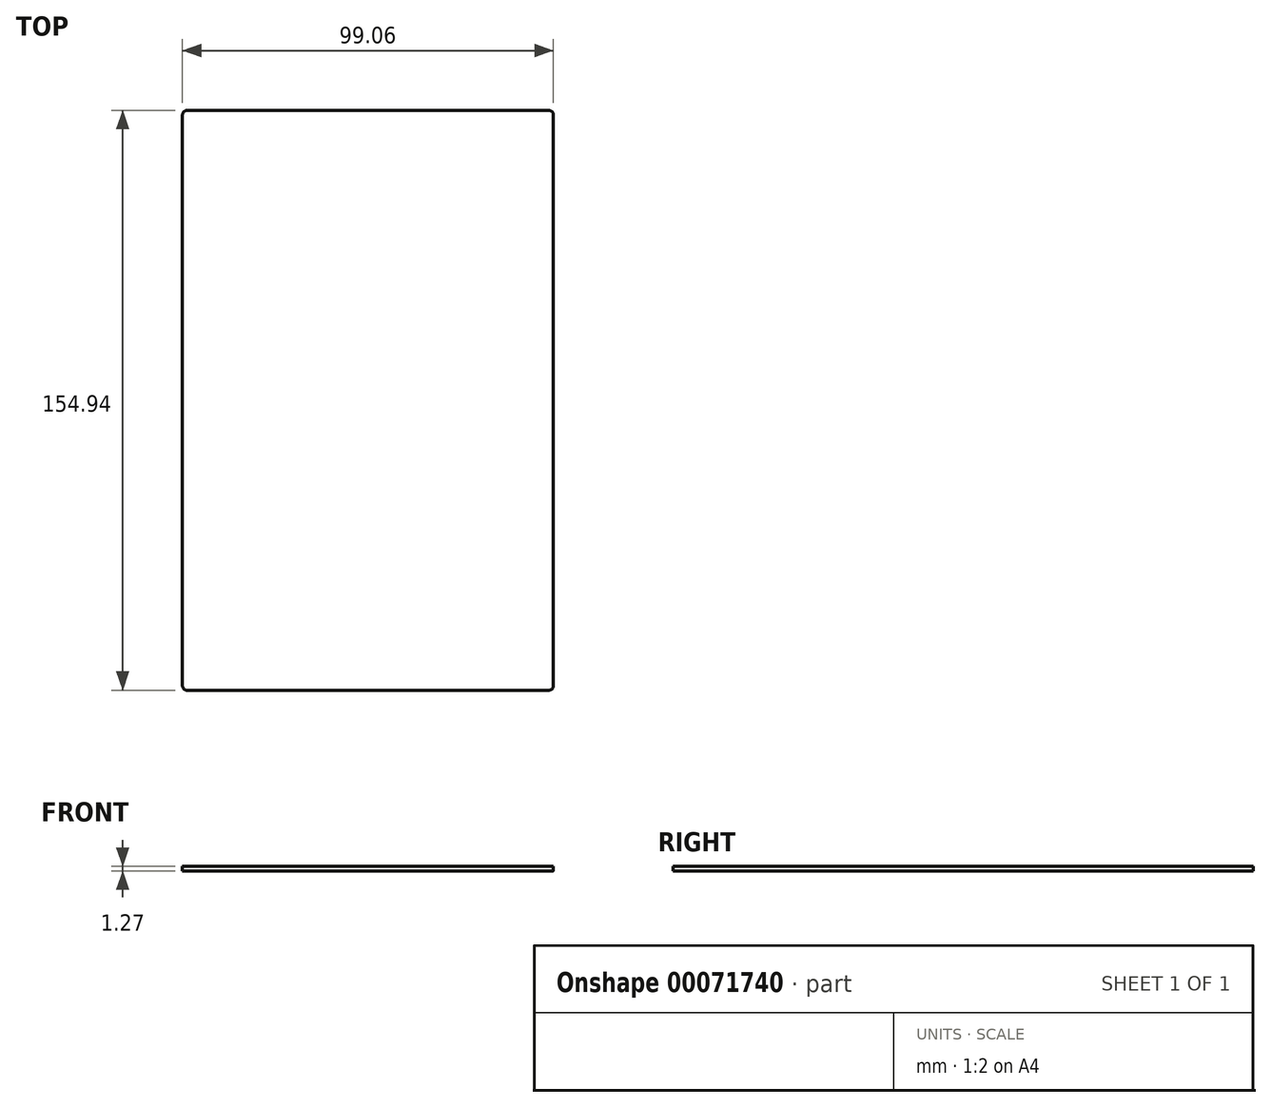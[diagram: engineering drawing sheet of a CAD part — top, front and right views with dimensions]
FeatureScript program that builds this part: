
annotation { "Feature Type Name" : "Feature", "Feature Type Description" : "" }
export const myFeature = defineFeature(function(context is Context, id is Id, definition is map)
    precondition{}
    {
        {
            var Q0;
            Q0=qCreatedBy(makeId("Top.planeOp"),FACE);
            var sketch = newSketch(context, id + "F0", { "sketchPlane" : qUnion([Q0])});
            skLineSegment(sketch, "E0.bottom", {"start": v(0, 0) * mm, "end": v(99.06, 0) * mm});
            skLineSegment(sketch, "E0.top", {"start": v(0, -154.94) * mm, "end": v(99.06, -154.94) * mm});
            skLineSegment(sketch, "E0.left", {"start": v(0, 0) * mm, "end": v(0, -154.94) * mm});
            skLineSegment(sketch, "E0.right", {"start": v(99.06, 0) * mm, "end": v(99.06, -154.94) * mm});
            skSolve(sketch);
        }
        {
            var Q0;
            Q0=makeQuery(id+"F0.imprint","IMPRINT",FACE,{"disambiguationData":[TD([[makeQuery(id+"F0.imprint","IMPRINT",EDGE,{"derivedFrom":sQuery(id+"F0.wireOp",EDGE,"E0.bottom")}),-1.0]])]});
            extrude(context, id + "F1", {"entities" : qUnion([Q0]), "depth" : 1.27 * mm});
        }
        {
            var Q0;
            Q0=makeQuery(id+"F1.opExtrude","SWEPT_EDGE",EDGE,{"disambiguationData":[OSD([sQuery(id+"F0.wireOp",EDGE,"E0.top"),sQuery(id+"F0.wireOp",EDGE,"E0.left")])]});
            var Q1;
            Q1=makeQuery(id+"F1.opExtrude","SWEPT_EDGE",EDGE,{"disambiguationData":[OSD([sQuery(id+"F0.wireOp",EDGE,"E0.top"),sQuery(id+"F0.wireOp",EDGE,"E0.right")])]});
            var Q2;
            Q2=makeQuery(id+"F1.opExtrude","SWEPT_EDGE",EDGE,{"disambiguationData":[OSD([sQuery(id+"F0.wireOp",EDGE,"E0.bottom"),sQuery(id+"F0.wireOp",EDGE,"E0.right")])]});
            var Q3;
            Q3=makeQuery(id+"F1.opExtrude","SWEPT_EDGE",EDGE,{"disambiguationData":[OSD([sQuery(id+"F0.wireOp",EDGE,"E0.bottom"),sQuery(id+"F0.wireOp",EDGE,"E0.left")])]});
            fillet(context, id + "F2", {"entities" : qUnion([Q0, Q1, Q2, Q3]), "radius" : 1.27 * mm, "tangentPropagation" : true, "allowEdgeOverflow" : false});
        }
    });
